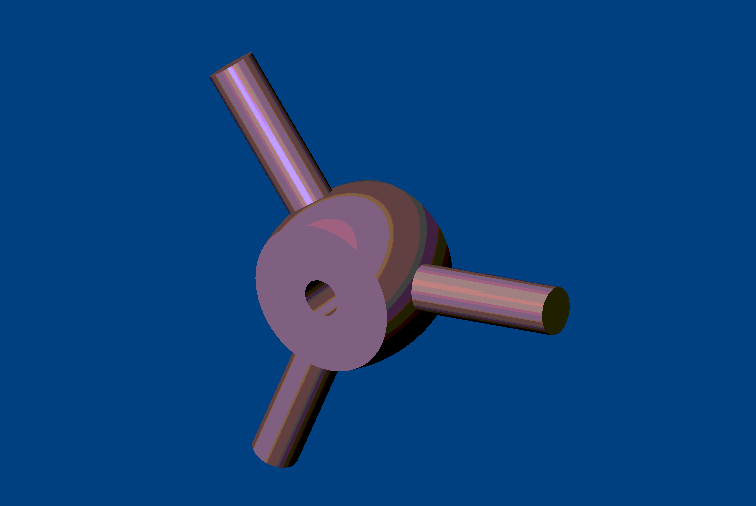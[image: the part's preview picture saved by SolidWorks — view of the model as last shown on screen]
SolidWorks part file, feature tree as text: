
SOLIDWORKS PART (.sldprt)
format: sldprt  version: not decoded by parser v0  size: 151,040 bytes
history: native  units: mm
features: plane x3, sketch x3, material x1, revolve x1, extrude x1, pattern_circular x1, cut_extrude x1 (+8 scaffold rows collapsed)
feature tree (19):
  scaffold x8  (default folders/planes/origin — collapsed)
  material  "Matériau <non spécifié>"
  plane  "Plane1"
  plane  "Plane2"
  plane  "Plane3"
  sketch  "Esquisse1"  dims[D1=20.0mm D2=5.5mm D3=3.0mm D4=3.0mm]
  revolve  "Base-Révolution"  Angle=360deg
  sketch  "Esquisse2"  dims[D1=2.0mm]
  sketch  "Esquisse3"  dims[D1=2.5mm]
  extrude  "Boss.-Extru.1"  Depth=12.5mm
  pattern_circular  "Répétition circulaire1"  Count=3  [1 undecoded]
  cut_extrude  "Enlèv. mat.-Extru.2"  [1 undecoded]
decode coverage: 6 of 7 modeling features carry decoded parameters
note: 2 parameter values undecoded
note: suppression state not decoded; provenance and decode notes live in map.json
